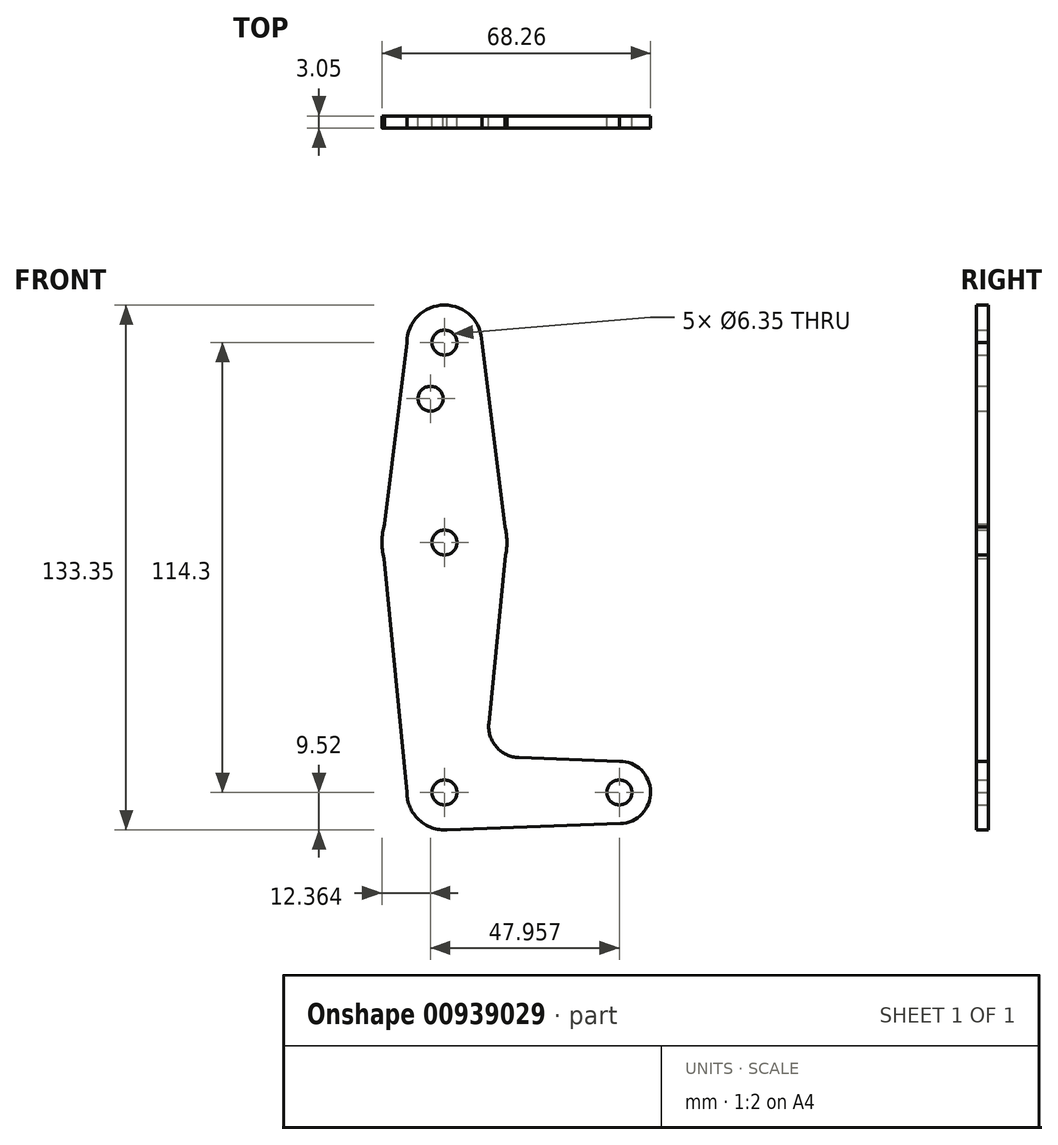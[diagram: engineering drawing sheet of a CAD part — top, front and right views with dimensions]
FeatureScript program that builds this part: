
annotation { "Feature Type Name" : "Feature", "Feature Type Description" : "" }
export const myFeature = defineFeature(function(context is Context, id is Id, definition is map)
    precondition{}
    {
        {
            var Q0;
            Q0=qCreatedBy(makeId("Front.planeOp"),FACE);
            var sketch = newSketch(context, id + "F0", { "sketchPlane" : qUnion([Q0])});
            skCircle(sketch, "E0", {"center": v(0, 0) * mm, "radius": 9.53 * mm});
            skCircle(sketch, "E1", {"center": v(44.44, 0) * mm, "radius": 7.94 * mm});
            skCircle(sketch, "E2", {"center": v(0, 63.5) * mm, "radius": 15.88 * mm});
            skCircle(sketch, "E3", {"center": v(0, 114.3) * mm, "radius": 9.53 * mm});
            skLineSegment(sketch, "E4", {"start": v(0, 114.3) * mm, "end": v(0, 63.5) * mm});
            skLineSegment(sketch, "E5", {"start": v(0, 63.5) * mm, "end": v(0, 0) * mm});
            skLineSegment(sketch, "E6", {"start": v(0, 0) * mm, "end": v(44.44, 0) * mm});
            skLineSegment(sketch, "E7", {"start": v(9.52, 114.3) * mm, "end": v(15.87, 63.5) * mm});
            skLineSegment(sketch, "E8", {"start": v(-9.52, 0) * mm, "end": v(-15.75, 63.5) * mm});
            skLineSegment(sketch, "E9", {"start": v(-9.53, 114.3) * mm, "end": v(-15.75, 63.5) * mm});
            skLineSegment(sketch, "E10", {"start": v(11.28, 17.59) * mm, "end": v(15.87, 63.5) * mm});
            skLineSegment(sketch, "E11", {"start": v(18.91, 8.85) * mm, "end": v(44.44, 7.94) * mm});
            skLineSegment(sketch, "E12", {"start": v(0, -9.53) * mm, "end": v(44.72, -7.93) * mm});
            skCircle(sketch, "E13", {"center": v(44.44, 0) * mm, "radius": 3.18 * mm});
            skCircle(sketch, "E14", {"center": v(0, 114.3) * mm, "radius": 3.18 * mm});
            skCircle(sketch, "E15", {"center": v(0, 63.5) * mm, "radius": 3.18 * mm});
            skCircle(sketch, "E16", {"center": v(0, 0) * mm, "radius": 3.18 * mm});
            skCircle(sketch, "E17", {"center": v(-3.52, 100.03) * mm, "radius": 3.18 * mm});
            skPoint(sketch, "E18.newPointA", {"position": v(9.52, 0) * mm});
            skArc(sketch, "E18.filletArc", {"start": v(11.28, 17.59) * mm, "mid": v(13.2, 11.57) * mm, "end": v(18.91, 8.85) * mm});
            skSolve(sketch);
        }
        {
            var Q0;
            Q0 = qSketchRegion(id + "F0", true);
            extrude(context, id + "F1", {"entities" : qUnion([Q0]), "depth" : 3.05 * mm, "offsetDistance" : 25.4 * mm});
        }
        {
            var Q0;
            {var subQ0=sQuery(id+"F0.wireOp",EDGE,"E5");var subQ1=sQuery(id+"F0.wireOp",EDGE,"E0");var subQ2=makeQuery(id+"F0.imprint","INTERSECT",VERTEX,{"derivedFrom":[subQ1,subQ0]});Q0=makeQuery(id+"F0.imprint","IMPRINT",FACE,{"disambiguationData":[TD([[makeQuery(id+"F0.imprint","IMPRINT",EDGE,{"disambiguationData":[TD([[subQ2,1.0]])],"derivedFrom":subQ1}),1.0]])]});}
            extrude(context, id + "F2", {"entities" : qUnion([Q0]), "operationType" : NewBodyOperationType.ADD, "depth" : 3.05 * mm, "offsetDistance" : 25.4 * mm});
        }
    });
